# Revit family: NLRS_56_ME_UN_climateceiling-kesa-3000-4000_LT_sacs
name_source: partatom
category: Mechanical Equipment
units: mm (PartAtom-declared; Revit-internal decimal feet)

## family parameters
Always vertical = Yes
Classification = None
Cut with Voids When Loaded = No
Maintain Annotation Orientation = No
OmniClass Number = 23.75.70.17.17
OmniClass Title = Radiation Panels
Part Type = Normal
Room Calculation Point = No
Round Connector Dimension = Use Diameter
Shared = No
Work Plane-Based = No

## types (3) — shared parameters
Assembly Code = 56.00
Default Elevation = 2700 mm  [stored 8.85827 ft]
Description = KESA Hybride Climate island
IfcDescription = KESA Hybride Climate island
IfcExportAs = IfcCoil
IfcExportType = IfcCoilType
Manufacturer = Solid Air Climate Solutions
Model = KESA
NLRS_C_content_datum_uitgifte = 03-06-2025
NLRS_C_content_provider = Solid Air Climate Solutions
NLRS_C_content_versie = 4.22.01
NLRS_C_description = KESA Hybride Climate island
SACS_Data_Hidden = KESA_Data
SACS_Dummy = 1
SACS_Type_Selector_1 = Base_Panel_KESA_R22 : Panel 9010-55
SACS_Type_Selector_2 = Base_Panel_KESA_R22 : Panel 9016-30
SACS_Type_Selector_3 = Base_Panel_KESA_R22 : Panel 9016-70
SACS_Type_Selector_4 = Base_Panel_KESA_R22 : Custom color
Type Comments = Islands with lengths 3000, 3500 and 4000
URL = https://solid-air-klimaatplafonds.nl

## per-type parameters (varying)
| type | SACS_Base_Index | SACS_Length_X | SACS_X_Offset |
| KESA 3000x1300 | 3 | 1194 mm | 210 mm  [stored 0.688976 ft] |
| KESA 3500x1300 | 4 | 1194 mm | 710 mm |
| KESA 4000x1300 | 5 | 1494 mm  [stored 4.90157 ft] | 610 mm  [stored 2.00131 ft] |

note: [stored X ft] marks values corroborated as IEEE doubles in the binary element streams (Revit-internal decimal feet)

## geometry (parser evidence)
native form markers: Sweep x12
no freeform markers — native parametric forms only
